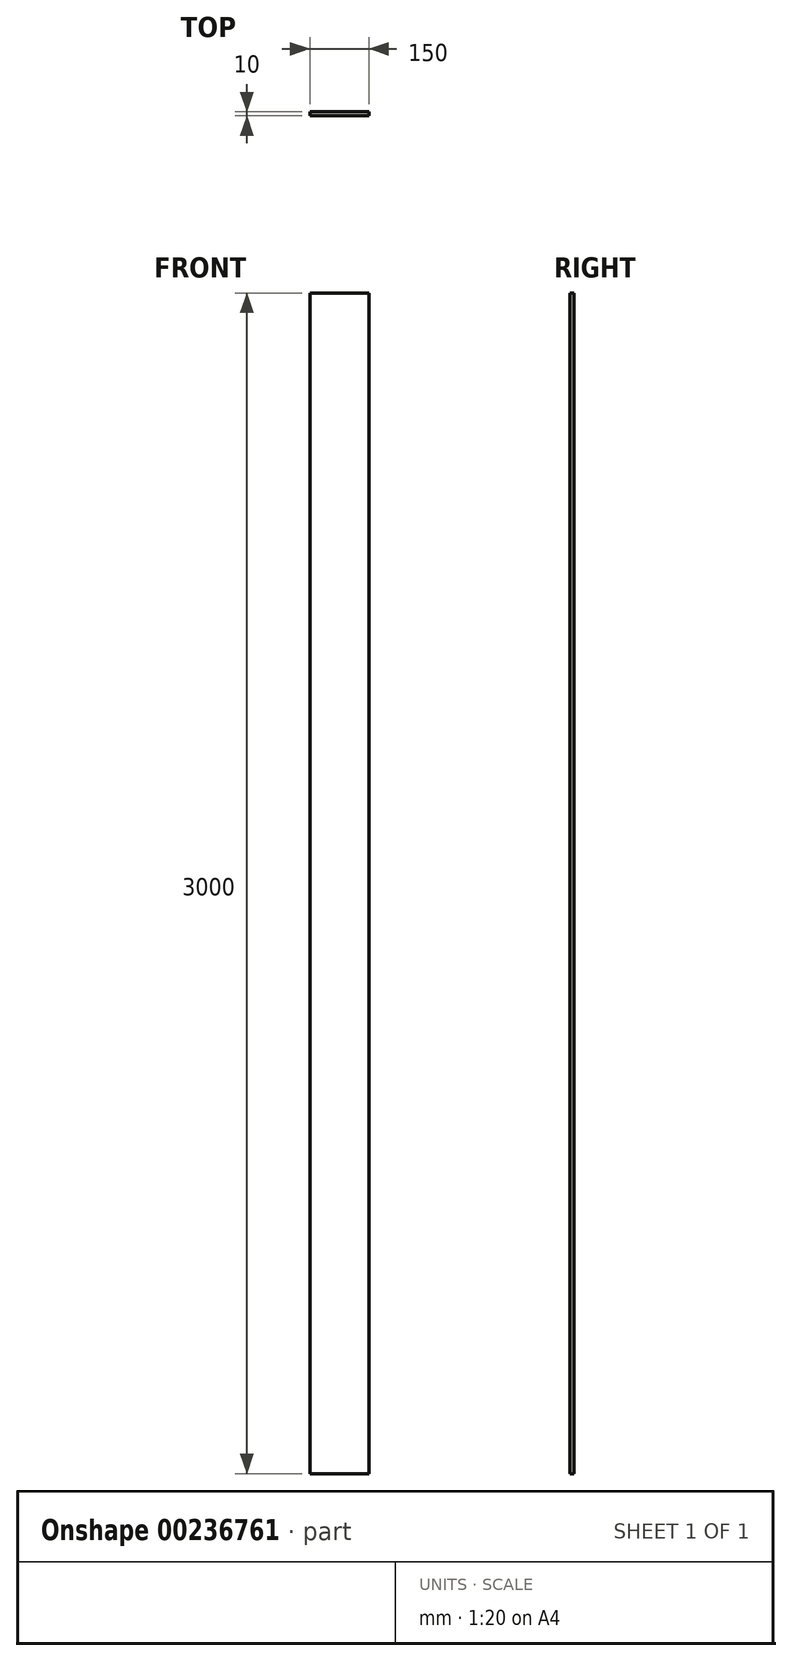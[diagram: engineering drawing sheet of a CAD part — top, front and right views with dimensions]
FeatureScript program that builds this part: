
annotation { "Feature Type Name" : "Feature", "Feature Type Description" : "" }
export const myFeature = defineFeature(function(context is Context, id is Id, definition is map)
    precondition{}
    {
        {
            var Q0;
            Q0=qCreatedBy(makeId("Top.planeOp"),FACE);
            var sketch = newSketch(context, id + "F0", { "sketchPlane" : qUnion([Q0])});
            skLineSegment(sketch, "E0.bottom", {"start": v(75, 0) * mm, "end": v(-75, 0) * mm});
            skLineSegment(sketch, "E0.top", {"start": v(75, 10) * mm, "end": v(-75, 10) * mm});
            skLineSegment(sketch, "E0.left", {"start": v(75, 0) * mm, "end": v(75, 10) * mm});
            skLineSegment(sketch, "E0.right", {"start": v(-75, 0) * mm, "end": v(-75, 10) * mm});
            skSolve(sketch);
        }
        {
            var Q0;
            Q0 = qSketchRegion(id + "F0", true);
            extrude(context, id + "F1", {"entities" : qUnion([Q0]), "depth" : 3000 * mm, "offsetDistance" : 25 * mm});
        }
    });
